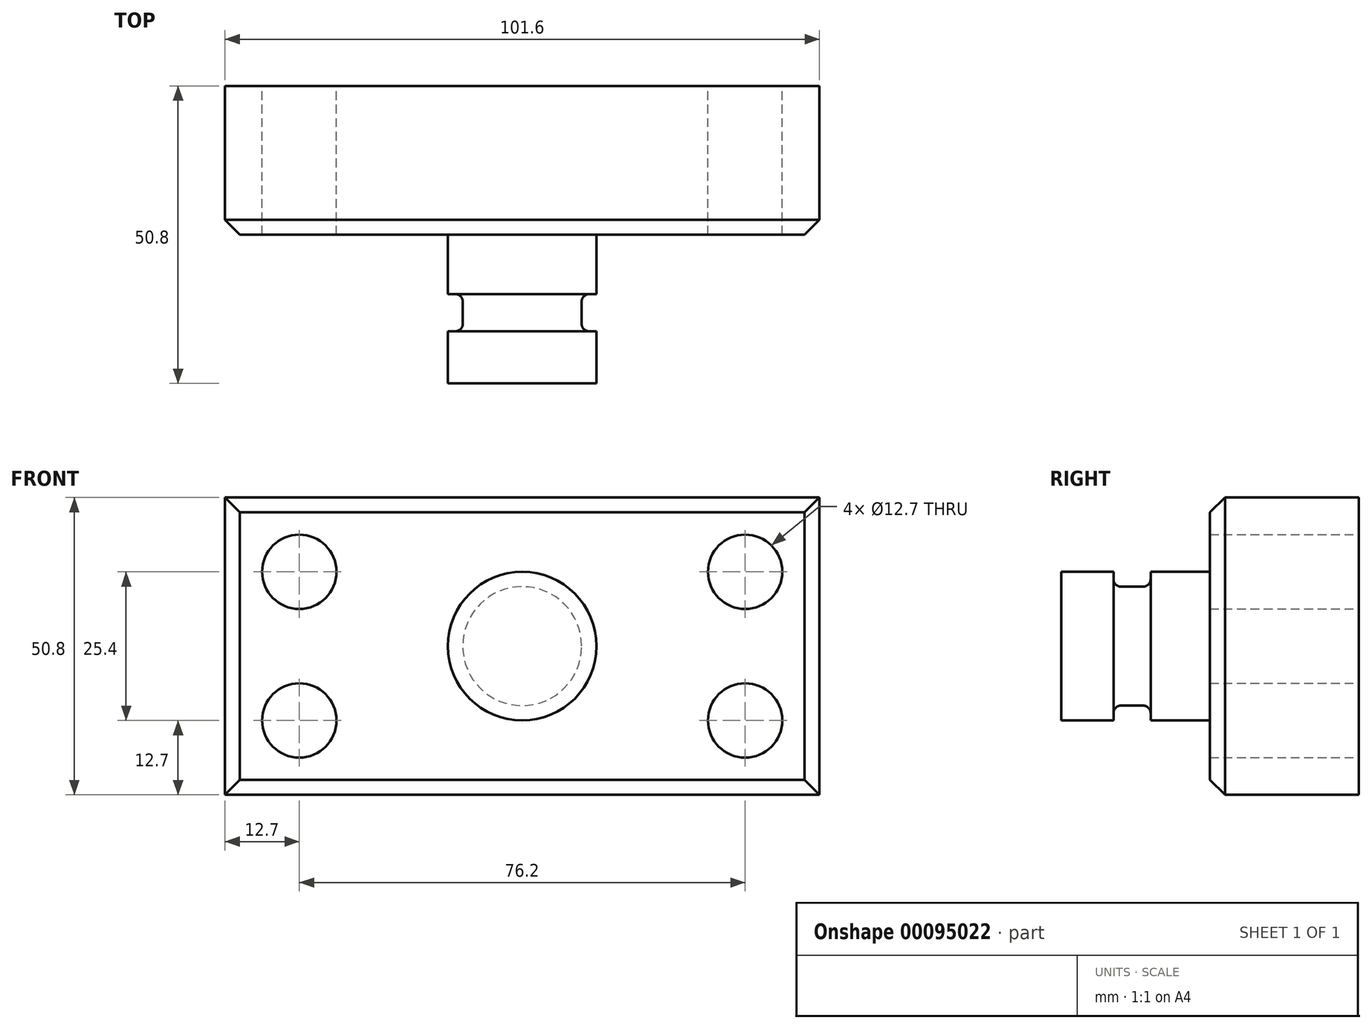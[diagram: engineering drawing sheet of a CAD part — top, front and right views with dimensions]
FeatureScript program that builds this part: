
annotation { "Feature Type Name" : "Feature", "Feature Type Description" : "" }
export const myFeature = defineFeature(function(context is Context, id is Id, definition is map)
    precondition{}
    {
        {
            var Q0;
            Q0=qCreatedBy(makeId("Front.planeOp"),FACE);
            var sketch = newSketch(context, id + "F0", { "sketchPlane" : qUnion([Q0])});
            skLineSegment(sketch, "E0.bottom", {"start": v(50.8, 25.4) * mm, "end": v(-50.8, 25.4) * mm});
            skLineSegment(sketch, "E0.top", {"start": v(50.8, -25.4) * mm, "end": v(-50.8, -25.4) * mm});
            skLineSegment(sketch, "E0.left", {"start": v(50.8, 25.4) * mm, "end": v(50.8, -25.4) * mm});
            skLineSegment(sketch, "E0.right", {"start": v(-50.8, 25.4) * mm, "end": v(-50.8, -25.4) * mm});
            skPoint(sketch, "E0.middle", {"position": v(0, 0) * mm});
            skSolve(sketch);
        }
        {
            var Q0;
            Q0=makeQuery(id+"F0.imprint","IMPRINT",FACE,{"disambiguationData":[TD([[makeQuery(id+"F0.imprint","IMPRINT",EDGE,{"derivedFrom":sQuery(id+"F0.wireOp",EDGE,"E0.bottom")}),1.0]])]});
            extrude(context, id + "F1", {"entities" : qUnion([Q0]), "depth" : 25.4 * mm});
        }
        {
            var Q0;
            Q0=makeQuery(id+"F1.opExtrude","CAP_FACE",FACE,{"disambiguationData":[OSD([sQuery(id+"F0.wireOp",EDGE,"E0.bottom"),sQuery(id+"F0.wireOp",EDGE,"E0.top"),sQuery(id+"F0.wireOp",EDGE,"E0.left"),sQuery(id+"F0.wireOp",EDGE,"E0.right")])],"isStart":true});
            var sketch = newSketch(context, id + "F2", { "sketchPlane" : qUnion([Q0])});
            skCircle(sketch, "E1", {"center": v(-38.1, 12.7) * mm, "radius": 6.35 * mm});
            skCircle(sketch, "E2", {"center": v(-38.1, -12.7) * mm, "radius": 6.35 * mm});
            skCircle(sketch, "E3", {"center": v(38.1, 12.7) * mm, "radius": 6.35 * mm});
            skCircle(sketch, "E4", {"center": v(38.1, -12.7) * mm, "radius": 6.35 * mm});
            skSolve(sketch);
        }
        {
            var Q0;
            Q0=makeQuery(id+"F2.imprint","IMPRINT",FACE,{"disambiguationData":[TD([[makeQuery(id+"F2.imprint","IMPRINT",EDGE,{"derivedFrom":sQuery(id+"F2.wireOp",EDGE,"E1")}),1.0]])]});
            var Q1;
            Q1=makeQuery(id+"F2.imprint","IMPRINT",FACE,{"disambiguationData":[TD([[makeQuery(id+"F2.imprint","IMPRINT",EDGE,{"derivedFrom":sQuery(id+"F2.wireOp",EDGE,"E2")}),1.0]])]});
            var Q2;
            Q2=makeQuery(id+"F2.imprint","IMPRINT",FACE,{"disambiguationData":[TD([[makeQuery(id+"F2.imprint","IMPRINT",EDGE,{"derivedFrom":sQuery(id+"F2.wireOp",EDGE,"E3")}),1.0]])]});
            var Q3;
            Q3=makeQuery(id+"F2.imprint","IMPRINT",FACE,{"disambiguationData":[TD([[makeQuery(id+"F2.imprint","IMPRINT",EDGE,{"derivedFrom":sQuery(id+"F2.wireOp",EDGE,"E4")}),1.0]])]});
            extrude(context, id + "F3", {"entities" : qUnion([Q0, Q1, Q2, Q3]), "operationType" : NewBodyOperationType.REMOVE, "endBound" : BoundingType.THROUGH_ALL, "oppositeDirection" : true, "depth" : 25.4 * mm});
        }
        {
            var Q0;
            Q0=qCreatedBy(makeId("Top.planeOp"),FACE);
            var sketch = newSketch(context, id + "F4", { "sketchPlane" : qUnion([Q0])});
            skLineSegment(sketch, "E5.bottom", {"start": v(0, -25.4) * mm, "end": v(-12.7, -25.4) * mm});
            skLineSegment(sketch, "E5.top", {"start": v(0, -50.8) * mm, "end": v(-12.7, -50.8) * mm});
            skLineSegment(sketch, "E5.left", {"start": v(0, -25.4) * mm, "end": v(0, -50.8) * mm});
            skLineSegment(sketch, "E5.right", {"start": v(-12.7, -25.4) * mm, "end": v(-12.7, -50.8) * mm});
            skSolve(sketch);
        }
        {
            var Q0;
            Q0 = qSketchRegion(id + "F4", true);
            var Q1;
            Q1=sQuery(id+"F4.wireOp",EDGE,"E5.left");
            revolve(context, id + "F5", {"operationType" : NewBodyOperationType.ADD, "entities" : qUnion([Q0]), "axis" : qUnion([Q1]), "revolveType" : RevolveType.FULL});
        }
        {
            var Q0;
            Q0=qCreatedBy(makeId("Top.planeOp"),FACE);
            var sketch = newSketch(context, id + "F6", { "sketchPlane" : qUnion([Q0])});
            skLineSegment(sketch, "E6.bottom", {"start": v(-16.02, -41.9) * mm, "end": v(-10.16, -41.9) * mm});
            skLineSegment(sketch, "E6.top", {"start": v(-16.02, -35.56) * mm, "end": v(-10.16, -35.56) * mm});
            skLineSegment(sketch, "E6.left", {"start": v(-16.02, -41.91) * mm, "end": v(-16.02, -35.56) * mm});
            skLineSegment(sketch, "E6.right", {"start": v(-10.16, -41.9) * mm, "end": v(-10.16, -35.56) * mm});
            skLineSegment(sketch, "E7", {"start": v(0, 5.56) * mm, "end": v(0, -63.87) * mm, "construction": true});
            skSolve(sketch);
        }
        {
            var Q0;
            Q0 = qSketchRegion(id + "F6", true);
            var Q1;
            Q1=sQuery(id+"F6.wireOp",EDGE,"E7");
            revolve(context, id + "F7", {"operationType" : NewBodyOperationType.REMOVE, "entities" : qUnion([Q0]), "axis" : qUnion([Q1]), "revolveType" : RevolveType.FULL, "oppositeDirection" : true});
        }
        {
            var Q0;
            Q0=makeQuery(id+"F5.opRevolve","SWEPT_EDGE",EDGE,{"disambiguationData":[OSD([sQuery(id+"F4.wireOp",EDGE,"E5.bottom"),sQuery(id+"F4.wireOp",EDGE,"E5.right")])]});
            var Q1;
            Q1=makeQuery(id+"F7.boolean.opBoolean","COPY",EDGE,{"derivedFrom":makeQuery(id+"F7.opRevolve","SWEPT_EDGE",EDGE,{"disambiguationData":[OSD([sQuery(id+"F6.wireOp",EDGE,"E6.bottom"),sQuery(id+"F6.wireOp",EDGE,"E6.right")])]})});
            var Q2;
            Q2=makeQuery(id+"F7.boolean.opBoolean","COPY",EDGE,{"derivedFrom":makeQuery(id+"F7.opRevolve","SWEPT_EDGE",EDGE,{"disambiguationData":[OSD([sQuery(id+"F6.wireOp",EDGE,"E6.top"),sQuery(id+"F6.wireOp",EDGE,"E6.right")])]})});
            fillet(context, id + "F8", {"entities" : qUnion([Q0, Q1, Q2]), "radius" : 1.27 * mm, "tangentPropagation" : true, "allowEdgeOverflow" : false});
        }
        {
            var Q0;
            Q0=makeQuery(id+"F1.opExtrude","CAP_EDGE",EDGE,{"disambiguationData":[OSD([sQuery(id+"F0.wireOp",EDGE,"E0.top")])],"isStart":false});
            var Q1;
            Q1=makeQuery(id+"F1.opExtrude","CAP_EDGE",EDGE,{"disambiguationData":[OSD([sQuery(id+"F0.wireOp",EDGE,"E0.left")])],"isStart":false});
            var Q2;
            Q2=makeQuery(id+"F1.opExtrude","CAP_EDGE",EDGE,{"disambiguationData":[OSD([sQuery(id+"F0.wireOp",EDGE,"E0.bottom")])],"isStart":false});
            var Q3;
            Q3=makeQuery(id+"F1.opExtrude","CAP_EDGE",EDGE,{"disambiguationData":[OSD([sQuery(id+"F0.wireOp",EDGE,"E0.right")])],"isStart":false});
            chamfer(context, id + "F9", {"entities" : qUnion([Q0, Q1, Q2, Q3]), "width" : 2.54 * mm, "tangentPropagation" : true});
        }
    });
